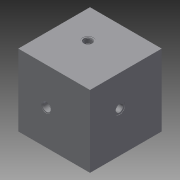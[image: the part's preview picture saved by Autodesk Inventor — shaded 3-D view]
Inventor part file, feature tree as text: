
AUTODESK INVENTOR PART (.ipt)
format: ipt  version: 2014 (Build 180170000, 170)  size: 360,448 bytes
history: native  units: mm
features: other x48, sketch x4, extrude x1
ambient origin geometry x8: Origin, YZ Plane, XZ Plane, XY Plane, X Axis, Y Axis, Z Axis, Center Point
bodies: 实体1 (feature_tree)
feature tree (53):
  extrude  "拉伸1"  TaperAngle=0.0deg  [1 undecoded]
  other  "UCS1"
  other  "UCS2"
  other  "UCS3"
  other  "UCS4"
  other  "UCS5"
  other  "UCS6"
  sketch  "草图1"  dims[d0=200.0mm d1=0.0mm]
  other  "UCS1: YZ 平面"
  other  "UCS1: XZ 平面"
  other  "UCS1: XY 平面"
  other  "UCS1: X 轴"
  other  "UCS1: Y 轴"
  other  "UCS1: Z 轴"
  other  "UCS1: 原点"
  other  "UCS2: YZ 平面"
  other  "UCS2: XZ 平面"
  other  "UCS2: XY 平面"
  other  "UCS2: X 轴"
  other  "UCS2: Y 轴"
  other  "UCS2: Z 轴"
  other  "UCS2: 原点"
  other  "UCS3: YZ 平面"
  other  "UCS3: XZ 平面"
  other  "UCS3: XY 平面"
  other  "UCS3: X 轴"
  other  "UCS3: Y 轴"
  other  "UCS3: Z 轴"
  other  "UCS3: 原点"
  other  "UCS4: YZ 平面"
  other  "UCS4: XZ 平面"
  other  "UCS4: XY 平面"
  other  "UCS4: X 轴"
  other  "UCS4: Y 轴"
  other  "UCS4: Z 轴"
  other  "UCS4: 原点"
  other  "UCS5: YZ 平面"
  other  "UCS5: XZ 平面"
  other  "UCS5: XY 平面"
  other  "UCS5: X 轴"
  other  "UCS5: Y 轴"
  other  "UCS5: Z 轴"
  other  "UCS5: 原点"
  other  "UCS6: YZ 平面"
  other  "UCS6: XZ 平面"
  other  "UCS6: XY 平面"
  other  "UCS6: X 轴"
  other  "UCS6: Y 轴"
  other  "UCS6: Z 轴"
  other  "UCS6: 原点"
  sketch  "草图2"  dims[d2=0.0mm d3=0.0mm d4=0.0mm d5=0.0mm d6=0.0mm d7=0.0mm]
  sketch  "草图3"  dims[d8=0.0mm d9=0.0mm d10=0.0mm d11=0.0mm d12=0.0mm d13=0.0mm]
  sketch  "草图4"  dims[d14=0.0mm d15=0.0mm d16=0.0mm d17=0.0mm d18=0.0mm d19=0.0mm d20=0.0mm d21=0.0mm d22=0.0mm d23=0.0mm d24=0.0mm d25=0.0mm d26=0.0mm d27=0.0mm d28=0.0mm d29=0.0mm d30=0.0mm d31=0.0mm d32=0.0mm d33=0.0mm d34=0.0mm d35=0.0mm d36=0.0mm d37=0.0mm d38=0.0mm d42=0.0mm d46=0.0mm d47=0.0mm d51=0.0mm d65=0.0mm d79=0.0mm d93=0.0mm d107=0.0mm d121=0.0mm d135=0.0mm]
note: 1 required parameter value undecoded (feature->parameter linkage not recoverable at this tier; creation-order binding heuristic only, values carry confidence <= 0.55)
